# Revit family: Clevertronics_FORM-16-SM-CM-RS-L10-HV_AUA01810980001
name_source: partatom
category: Lighting Fixtures
units: mm (PartAtom-declared; Revit-internal decimal feet)

## family parameters
Cut with Voids When Loaded = No
Host = Face
Light Source = No
OmniClass Number = 23.80.70.11.21
OmniClass Title = Emergency Lighting
Part Type = Normal
Room Calculation Point = No
Round Connector Dimension = Use Diameter
Shared = No

## types (5) — shared parameters
3D Content Provider = Mepros engineering
Apparent Load = 0 VA
Clevertronics_Applicable Standards = AS/NZS3820, CISPR15, AS/NZS2293.3
Clevertronics_Battery = 3.3V 2500mAh
Clevertronics_Battery Type = Lithium Nanophosphate
Clevertronics_Charger Method = Intelligent Current Limited Constant Voltage
Clevertronics_Construction = Cast Aluminium Box with PC/Aluminium Extrusion Blade
Clevertronics_Diffuser = Polycarbonate
Clevertronics_Dimensions Main Enclosure = 210mm x 52mm x 100mm
Clevertronics_Earth Leakage = 0.35mA
Clevertronics_Electrical Connection = Screw Terminal
Clevertronics_Emergency Driver = Emergency Driver : AUM01870790001
Clevertronics_Emergency Node = HIVE Node : 8003182
Clevertronics_IK Rating = IK03
Clevertronics_IP Rating = IP20
Clevertronics_Inrush Current (Max) = 10A<144μs
Clevertronics_MIC Number = AUA01810980001
Clevertronics_Mounting = Surface Ceiling Mount, Double Sided
Clevertronics_Operating Mode = Maintained
Clevertronics_Operating Temperature = 1 ºC to 40ºC
Clevertronics_Operating Voltage = 220-240V~ 50Hz
Clevertronics_Power Consumption = 1.5W (Standby), 3.6W (Max)
Clevertronics_Power Factor = 0.28 (Standby, Maintained), 0.42 (Max)
Clevertronics_Product Description = Form 16M Exit, Surface Ceiling Mount, Rod Suspended, L10 Nanophosphate, Zoneworks XT Hive, All Pictograms, Double Sided, Brushed Aluminium Frame
Clevertronics_Replacement Battery = Battery : 1530050
Clevertronics_Supply Current = 19.91 (Standby, Maintained), 35.60 (Max) - (mA)
Clevertronics_Testing System = Zoneworks XT HIVE (RF)
Clevertronics_Viewing Distance = 16m
Clevertronics_Weight = 1.30kg
Content Provider URL = https://mepros-eng.com
Description = Form 16M Exit, Surface Ceiling Mount, Rod Suspended, L10 Nanophosphate, Zoneworks XT Hive, All Pictograms, Double Sided, Brushed Aluminium Frame
Lamp = 18 x LED, >100,000hrs (AS/NZS2293.3 LSL=73Y/00M)
Manufacturer = Clevertronics
Material = Clevertronics_White
Model = FORM-16-SM-CM-RS-L10-HV
Product URL = https://clevertronics.com.au
URL = https://clevertronics.com.au
zero-valued in all types: Default Elevation

## per-type parameters (varying)
| type | Indication Left | Indication Right | RM Side (DS) | Straight Line (DS) | Straight line |
| Running Man Single | No | No | No | No | Yes |
| Runnign Man Common arrow (double side) | No | No | Yes | No | No |
| Running Man (Double side) | No | No | No | Yes | Yes |
| Running Man Left (Single) | Yes | No | No | No | No |
| Running Man Right (Single) | No | Yes | No | No | No |

## geometry (parser evidence)
native form markers: Blend x2, Extrusion x12, Sweep x3
no freeform markers — native parametric forms only
